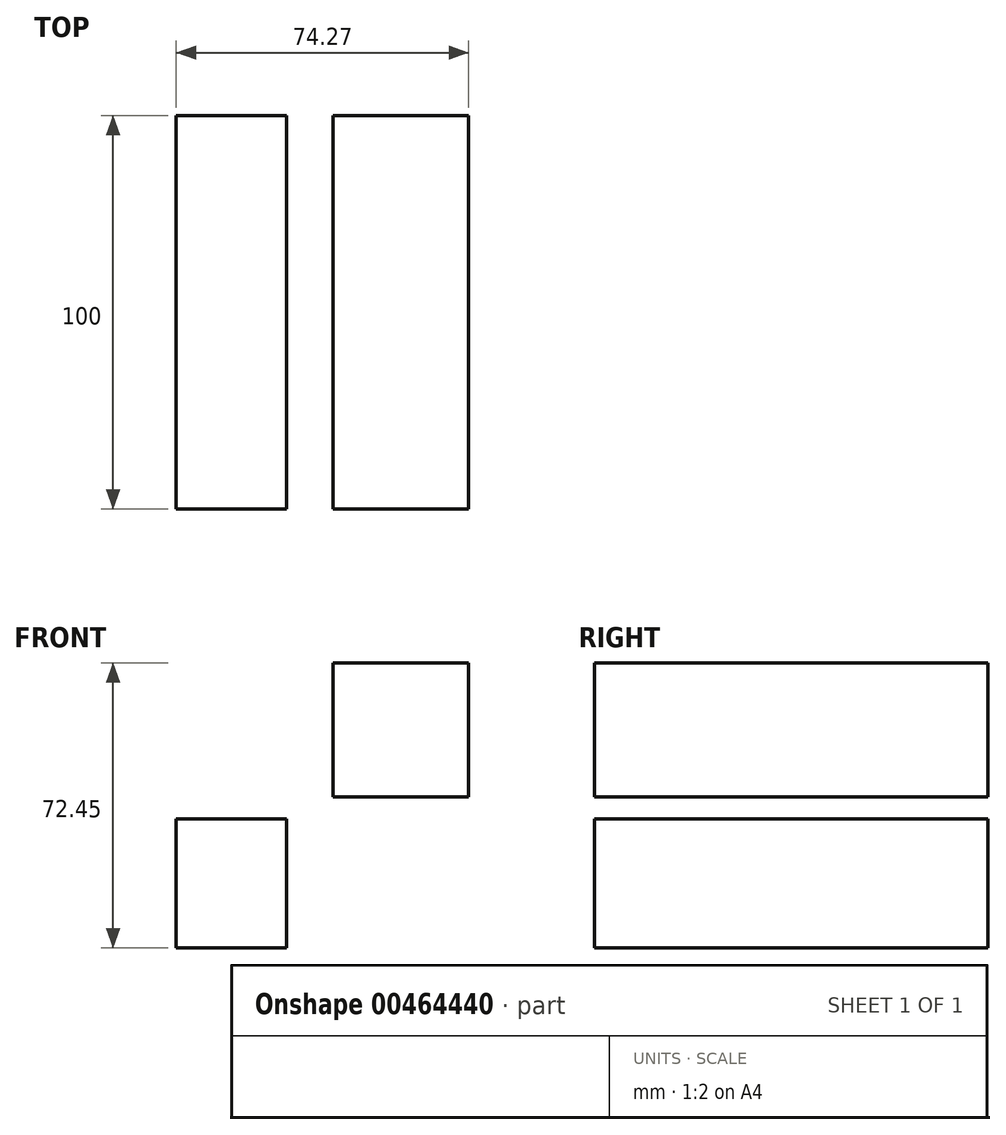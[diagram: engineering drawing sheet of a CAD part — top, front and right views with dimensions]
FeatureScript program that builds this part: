
annotation { "Feature Type Name" : "Feature", "Feature Type Description" : "" }
export const myFeature = defineFeature(function(context is Context, id is Id, definition is map)
    precondition{}
    {
        {
            var Q0;
            Q0=qCreatedBy(makeId("Front.planeOp"),FACE);
            var sketch = newSketch(context, id + "F0", { "sketchPlane" : qUnion([Q0])});
            skLineSegment(sketch, "E0.bottom", {"start": v(-17.19, 17.05) * mm, "end": v(17.19, 17.05) * mm});
            skLineSegment(sketch, "E0.top", {"start": v(-17.19, -17.05) * mm, "end": v(17.19, -17.05) * mm});
            skLineSegment(sketch, "E0.left", {"start": v(-17.19, 17.05) * mm, "end": v(-17.19, -17.05) * mm});
            skLineSegment(sketch, "E0.right", {"start": v(17.19, 17.05) * mm, "end": v(17.19, -17.05) * mm});
            skPoint(sketch, "E0.middle", {"position": v(0, 0) * mm});
            skSolve(sketch);
        }
        {
            var Q0;
            Q0=makeQuery(id+"F0.imprint","IMPRINT",FACE,{"disambiguationData":[TD([[makeQuery(id+"F0.imprint","IMPRINT",EDGE,{"derivedFrom":sQuery(id+"F0.wireOp",EDGE,"E0.bottom")}),-1.0]])]});
            extrude(context, id + "F1", {"entities" : qUnion([Q0]), "depth" : 100 * mm});
        }
        {
            var Q0;
            Q0=qCreatedBy(makeId("Front.planeOp"),FACE);
            var sketch = newSketch(context, id + "F2", { "sketchPlane" : qUnion([Q0])});
            skLineSegment(sketch, "E1.bottom", {"start": v(-29, -55.4) * mm, "end": v(-57.08, -55.4) * mm});
            skLineSegment(sketch, "E1.top", {"start": v(-29, -22.65) * mm, "end": v(-57.08, -22.65) * mm});
            skLineSegment(sketch, "E1.left", {"start": v(-29, -55.4) * mm, "end": v(-29, -22.65) * mm});
            skLineSegment(sketch, "E1.right", {"start": v(-57.08, -55.4) * mm, "end": v(-57.08, -22.65) * mm});
            skPoint(sketch, "E1.middle", {"position": v(-43.04, -39.03) * mm});
            skLineSegment(sketch, "E2.bottom", {"start": v(-48.2, -55.4) * mm, "end": v(-9.8, -55.4) * mm});
            skLineSegment(sketch, "E2.top", {"start": v(-48.2, -55.4) * mm, "end": v(-9.8, -55.4) * mm});
            skLineSegment(sketch, "E2.left", {"start": v(-48.2, -55.4) * mm, "end": v(-48.2, -55.4) * mm});
            skLineSegment(sketch, "E2.right", {"start": v(-9.8, -55.4) * mm, "end": v(-9.8, -55.4) * mm});
            skPoint(sketch, "E2.middle", {"position": v(-29, -55.4) * mm});
            skSolve(sketch);
        }
        {
            var Q0;
            Q0 = qSketchRegion(id + "F2", true);
            var Q1;
            {var subQ1=sQuery(id+"F2.wireOp",EDGE,"E1.bottom");Q1=makeQuery(id+"F2.imprint","IMPRINT",FACE,{"disambiguationData":[TD([[makeQuery(id+"F2.imprint","IMPRINT",EDGE,{"derivedFrom":subQ1}),-1.0]])]});}
            extrude(context, id + "F3", {"entities" : qUnion([Q0, Q1]), "depth" : 100 * mm});
        }
    });
